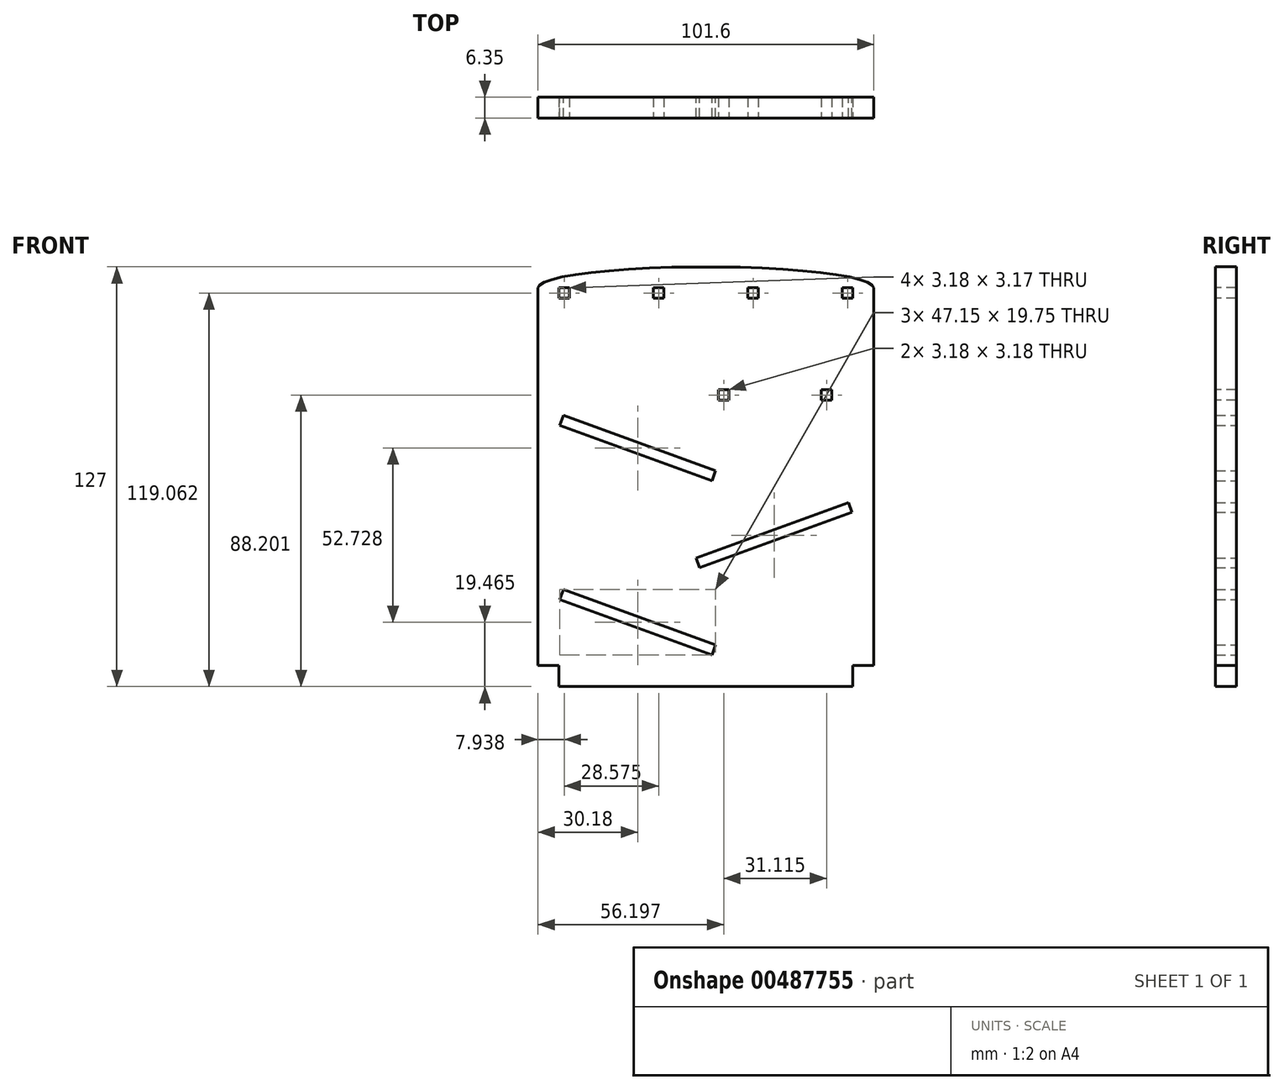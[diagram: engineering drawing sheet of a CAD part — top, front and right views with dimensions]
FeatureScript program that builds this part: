
annotation { "Feature Type Name" : "Feature", "Feature Type Description" : "" }
export const myFeature = defineFeature(function(context is Context, id is Id, definition is map)
    precondition{}
    {
        {
            var Q0;
            Q0=qCreatedBy(makeId("Front.planeOp"),FACE);
            var sketch = newSketch(context, id + "F0", { "sketchPlane" : qUnion([Q0])});
            skLineSegment(sketch, "E0.bottom", {"start": v(-50.8, 63.5) * mm, "end": v(50.8, 63.5) * mm});
            skLineSegment(sketch, "E0.top", {"start": v(-50.8, -63.5) * mm, "end": v(50.8, -63.5) * mm});
            skLineSegment(sketch, "E0.left", {"start": v(-50.8, 63.5) * mm, "end": v(-50.8, -63.5) * mm});
            skLineSegment(sketch, "E0.right", {"start": v(50.8, 63.5) * mm, "end": v(50.8, -63.5) * mm});
            skPoint(sketch, "E0.middle", {"position": v(0, 0) * mm});
            skSolve(sketch);
        }
        {
            var Q0;
            Q0 = qSketchRegion(id + "F0", true);
            extrude(context, id + "F1", {"entities" : qUnion([Q0]), "depth" : 6.35 * mm});
        }
        {
            var Q0;
            Q0=makeQuery(id+"F1.opExtrude","CAP_FACE",FACE,{"disambiguationData":[OSD([sQuery(id+"F0.wireOp",EDGE,"E0.bottom"),sQuery(id+"F0.wireOp",EDGE,"E0.top"),sQuery(id+"F0.wireOp",EDGE,"E0.left"),sQuery(id+"F0.wireOp",EDGE,"E0.right")])],"isStart":false});
            var sketch = newSketch(context, id + "F2", { "sketchPlane" : qUnion([Q0])});
            skLineSegment(sketch, "E1.bottom", {"start": v(-50.8, 63.5) * mm, "end": v(50.8, 63.5) * mm});
            skLineSegment(sketch, "E1.top", {"start": v(-50.8, 57.15) * mm, "end": v(50.8, 57.15) * mm});
            skLineSegment(sketch, "E1.left", {"start": v(-50.8, 63.5) * mm, "end": v(-50.8, 57.15) * mm});
            skLineSegment(sketch, "E1.right", {"start": v(50.8, 63.5) * mm, "end": v(50.8, 57.15) * mm});
            skLineSegment(sketch, "E2.bottom", {"start": v(-50.8, 57.15) * mm, "end": v(-44.45, 57.15) * mm});
            skLineSegment(sketch, "E2.top", {"start": v(-50.8, 50.8) * mm, "end": v(-44.45, 50.8) * mm});
            skLineSegment(sketch, "E2.left", {"start": v(-50.8, 57.15) * mm, "end": v(-50.8, 50.8) * mm});
            skLineSegment(sketch, "E2.right", {"start": v(-44.45, 57.15) * mm, "end": v(-44.45, 50.8) * mm});
            skLineSegment(sketch, "E3.bottom", {"start": v(-50.8, -63.5) * mm, "end": v(-44.45, -63.5) * mm});
            skLineSegment(sketch, "E3.top", {"start": v(-50.8, -57.15) * mm, "end": v(-44.45, -57.15) * mm});
            skLineSegment(sketch, "E3.left", {"start": v(-50.8, -63.5) * mm, "end": v(-50.8, -57.15) * mm});
            skLineSegment(sketch, "E3.right", {"start": v(-44.45, -63.5) * mm, "end": v(-44.45, -57.15) * mm});
            skLineSegment(sketch, "E4.bottom", {"start": v(50.8, -63.5) * mm, "end": v(44.45, -63.5) * mm});
            skLineSegment(sketch, "E4.top", {"start": v(50.8, -57.15) * mm, "end": v(44.45, -57.15) * mm});
            skLineSegment(sketch, "E4.left", {"start": v(50.8, -63.5) * mm, "end": v(50.8, -57.15) * mm});
            skLineSegment(sketch, "E4.right", {"start": v(44.45, -63.5) * mm, "end": v(44.45, -57.15) * mm});
            skLineSegment(sketch, "E5.bottom", {"start": v(50.8, 57.15) * mm, "end": v(44.45, 57.15) * mm});
            skLineSegment(sketch, "E5.top", {"start": v(50.8, 50.8) * mm, "end": v(44.45, 50.8) * mm});
            skLineSegment(sketch, "E5.left", {"start": v(50.8, 57.15) * mm, "end": v(50.8, 50.8) * mm});
            skLineSegment(sketch, "E5.right", {"start": v(44.45, 57.15) * mm, "end": v(44.45, 50.8) * mm});
            skSolve(sketch);
        }
        {
            var Q0;
            Q0=makeQuery(id+"F2.imprint","IMPRINT",FACE,{"disambiguationData":[TD([[makeQuery(id+"F2.imprint","IMPRINT",EDGE,{"derivedFrom":sQuery(id+"F2.wireOp",EDGE,"E2.bottom")}),-1.0]])]});
            var Q1;
            Q1=makeQuery(id+"F2.imprint","IMPRINT",FACE,{"disambiguationData":[TD([[makeQuery(id+"F2.imprint","IMPRINT",EDGE,{"derivedFrom":sQuery(id+"F2.wireOp",EDGE,"E5.bottom")}),1.0]])]});
            var Q2;
            Q2=makeQuery(id+"F2.imprint","IMPRINT",FACE,{"disambiguationData":[TD([[makeQuery(id+"F2.imprint","IMPRINT",EDGE,{"derivedFrom":sQuery(id+"F2.wireOp",EDGE,"E4.bottom")}),1.0]])]});
            var Q3;
            Q3=makeQuery(id+"F2.imprint","IMPRINT",FACE,{"disambiguationData":[TD([[makeQuery(id+"F2.imprint","IMPRINT",EDGE,{"derivedFrom":sQuery(id+"F2.wireOp",EDGE,"E3.bottom")}),1.0]])]});
            extrude(context, id + "F3", {"entities" : qUnion([Q0, Q1, Q2, Q3]), "operationType" : NewBodyOperationType.REMOVE, "endBound" : BoundingType.THROUGH_ALL, "oppositeDirection" : true, "depth" : 6.35 * mm});
        }
        {
            var Q0;
            Q0=makeQuery(id+"F1.opExtrude","CAP_FACE",FACE,{"disambiguationData":[OSD([sQuery(id+"F0.wireOp",EDGE,"E0.bottom"),sQuery(id+"F0.wireOp",EDGE,"E0.top"),sQuery(id+"F0.wireOp",EDGE,"E0.left"),sQuery(id+"F0.wireOp",EDGE,"E0.right")])],"isStart":false});
            var sketch = newSketch(context, id + "F4", { "sketchPlane" : qUnion([Q0])});
            skLineSegment(sketch, "E6.bottom", {"start": v(-44.45, 57.15) * mm, "end": v(44.45, 57.15) * mm});
            skLineSegment(sketch, "E6.top", {"start": v(-44.45, 50.8) * mm, "end": v(44.45, 50.8) * mm});
            skLineSegment(sketch, "E6.left", {"start": v(-44.45, 57.15) * mm, "end": v(-44.45, 50.8) * mm});
            skLineSegment(sketch, "E6.right", {"start": v(44.45, 57.15) * mm, "end": v(44.45, 50.8) * mm});
            skEllipse(sketch, "E7", {"center": v(0, 57.15) * mm, "majorRadius": 50.8 * mm, "minorRadius": 6.35 * mm, "majorAxis": v(-1, 0)});
            skSolve(sketch);
        }
        {
            var Q0;
            {var subQ1=sQuery(id+"F0.wireOp",EDGE,"E0.bottom");var subQ2=sQuery(id+"F0.wireOp",EDGE,"E0.left");var subQ4=makeQuery(id+"F3.boolean.opBoolean","SPLIT",EDGE,{"disambiguationData":[TD([makeQuery(id+"F1.opExtrude","SWEPT_FACE",FACE,{"disambiguationData":[OSD([subQ1])]})])],"derivedFrom":makeQuery(id+"F1.opExtrude","CAP_EDGE",EDGE,{"disambiguationData":[OSD([subQ2])],"isStart":false})});Q0=makeQuery(id+"F4.imprint","IMPRINT",FACE,{"disambiguationData":[TD([[makeQuery(id+"F4.imprint","IMPRINT",EDGE,{"derivedFrom":subQ4}),1.0]])]});}
            var Q1;
            {var subQ1=sQuery(id+"F0.wireOp",EDGE,"E0.bottom");var subQ2=sQuery(id+"F0.wireOp",EDGE,"E0.right");var subQ4=makeQuery(id+"F3.boolean.opBoolean","SPLIT",EDGE,{"disambiguationData":[TD([makeQuery(id+"F1.opExtrude","SWEPT_FACE",FACE,{"disambiguationData":[OSD([subQ1])]})])],"derivedFrom":makeQuery(id+"F1.opExtrude","CAP_EDGE",EDGE,{"disambiguationData":[OSD([subQ2])],"isStart":false})});Q1=makeQuery(id+"F4.imprint","IMPRINT",FACE,{"disambiguationData":[TD([[makeQuery(id+"F4.imprint","IMPRINT",EDGE,{"derivedFrom":subQ4}),-1.0]])]});}
            extrude(context, id + "F5", {"entities" : qUnion([Q0, Q1]), "operationType" : NewBodyOperationType.REMOVE, "endBound" : BoundingType.THROUGH_ALL, "oppositeDirection" : true, "depth" : 25.4 * mm});
        }
        {
            var Q0;
            Q0=makeQuery(id+"F1.opExtrude","CAP_FACE",FACE,{"disambiguationData":[OSD([sQuery(id+"F0.wireOp",EDGE,"E0.bottom"),sQuery(id+"F0.wireOp",EDGE,"E0.top"),sQuery(id+"F0.wireOp",EDGE,"E0.left"),sQuery(id+"F0.wireOp",EDGE,"E0.right")])],"isStart":false});
            var sketch = newSketch(context, id + "F6", { "sketchPlane" : qUnion([Q0])});
            skPoint(sketch, "E8.oppositeSnap0", {"position": v(-44.45, 53.98) * mm});
            skLineSegment(sketch, "E8.bottom", {"start": v(-44.45, 57.15) * mm, "end": v(-41.28, 57.15) * mm});
            skLineSegment(sketch, "E8.top", {"start": v(-44.45, 53.98) * mm, "end": v(-41.28, 53.98) * mm});
            skLineSegment(sketch, "E8.left", {"start": v(-44.45, 57.15) * mm, "end": v(-44.45, 53.98) * mm});
            skLineSegment(sketch, "E8.right", {"start": v(-41.28, 57.15) * mm, "end": v(-41.28, 53.98) * mm});
            skLineSegment(sketch, "E9.bottom", {"start": v(-15.87, 57.15) * mm, "end": v(-12.7, 57.15) * mm});
            skLineSegment(sketch, "E9.top", {"start": v(-15.87, 53.98) * mm, "end": v(-12.7, 53.98) * mm});
            skLineSegment(sketch, "E9.left", {"start": v(-15.87, 57.15) * mm, "end": v(-15.87, 53.98) * mm});
            skLineSegment(sketch, "E9.right", {"start": v(-12.7, 57.15) * mm, "end": v(-12.7, 53.98) * mm});
            skLineSegment(sketch, "E10.bottom", {"start": v(12.7, 57.15) * mm, "end": v(15.88, 57.15) * mm});
            skLineSegment(sketch, "E10.top", {"start": v(12.7, 53.98) * mm, "end": v(15.88, 53.98) * mm});
            skLineSegment(sketch, "E10.left", {"start": v(12.7, 57.15) * mm, "end": v(12.7, 53.98) * mm});
            skLineSegment(sketch, "E10.right", {"start": v(15.88, 57.15) * mm, "end": v(15.88, 53.98) * mm});
            skLineSegment(sketch, "E11.bottom", {"start": v(41.28, 57.15) * mm, "end": v(44.45, 57.15) * mm});
            skLineSegment(sketch, "E11.top", {"start": v(41.28, 53.98) * mm, "end": v(44.45, 53.98) * mm});
            skLineSegment(sketch, "E11.left", {"start": v(41.28, 57.15) * mm, "end": v(41.28, 53.98) * mm});
            skLineSegment(sketch, "E11.right", {"start": v(44.45, 57.15) * mm, "end": v(44.45, 53.98) * mm});
            skLineSegment(sketch, "E12", {"start": v(6.99, 26.29) * mm, "end": v(34.93, 26.29) * mm});
            skLineSegment(sketch, "E13.bottom", {"start": v(34.93, 26.29) * mm, "end": v(38.1, 26.29) * mm});
            skLineSegment(sketch, "E13.top", {"start": v(34.93, 23.11) * mm, "end": v(38.1, 23.11) * mm});
            skLineSegment(sketch, "E13.left", {"start": v(34.93, 26.29) * mm, "end": v(34.93, 23.11) * mm});
            skLineSegment(sketch, "E13.right", {"start": v(38.1, 26.29) * mm, "end": v(38.1, 23.11) * mm});
            skLineSegment(sketch, "E14.bottom", {"start": v(6.99, 26.29) * mm, "end": v(3.8, 26.29) * mm});
            skLineSegment(sketch, "E14.top", {"start": v(6.99, 23.11) * mm, "end": v(3.81, 23.11) * mm});
            skLineSegment(sketch, "E14.left", {"start": v(6.99, 26.29) * mm, "end": v(6.99, 23.11) * mm});
            skLineSegment(sketch, "E14.right", {"start": v(3.8, 26.29) * mm, "end": v(3.81, 23.11) * mm});
            skSolve(sketch);
        }
        {
            var Q0;
            Q0=makeQuery(id+"F6.imprint","IMPRINT",FACE,{"disambiguationData":[TD([[makeQuery(id+"F6.imprint","IMPRINT",EDGE,{"derivedFrom":sQuery(id+"F6.wireOp",EDGE,"E8.bottom")}),-1.0]])]});
            var Q1;
            Q1=makeQuery(id+"F6.imprint","IMPRINT",FACE,{"disambiguationData":[TD([[makeQuery(id+"F6.imprint","IMPRINT",EDGE,{"derivedFrom":sQuery(id+"F6.wireOp",EDGE,"E9.bottom")}),-1.0]])]});
            var Q2;
            Q2=makeQuery(id+"F6.imprint","IMPRINT",FACE,{"disambiguationData":[TD([[makeQuery(id+"F6.imprint","IMPRINT",EDGE,{"derivedFrom":sQuery(id+"F6.wireOp",EDGE,"E10.bottom")}),-1.0]])]});
            var Q3;
            Q3=makeQuery(id+"F6.imprint","IMPRINT",FACE,{"disambiguationData":[TD([[makeQuery(id+"F6.imprint","IMPRINT",EDGE,{"derivedFrom":sQuery(id+"F6.wireOp",EDGE,"E11.bottom")}),-1.0]])]});
            var Q4;
            Q4=makeQuery(id+"F6.imprint","IMPRINT",FACE,{"disambiguationData":[TD([[makeQuery(id+"F6.imprint","IMPRINT",EDGE,{"derivedFrom":sQuery(id+"F6.wireOp",EDGE,"E13.bottom")}),-1.0]])]});
            var Q5;
            Q5=makeQuery(id+"F6.imprint","IMPRINT",FACE,{"disambiguationData":[TD([[makeQuery(id+"F6.imprint","IMPRINT",EDGE,{"derivedFrom":sQuery(id+"F6.wireOp",EDGE,"E14.bottom")}),1.0]])]});
            extrude(context, id + "F7", {"entities" : qUnion([Q0, Q1, Q2, Q3, Q4, Q5]), "operationType" : NewBodyOperationType.REMOVE, "endBound" : BoundingType.THROUGH_ALL, "oppositeDirection" : true, "depth" : 25.4 * mm});
        }
        {
            var Q0;
            Q0=qCreatedBy(makeId("Front.planeOp"),FACE);
            var sketch = newSketch(context, id + "F8", { "sketchPlane" : qUnion([Q0])});
            skLineSegment(sketch, "E15", {"start": v(-43.11, 18.57) * mm, "end": v(2.96, 1.8) * mm});
            skLineSegment(sketch, "E16", {"start": v(2.96, 1.8) * mm, "end": v(1.87, -1.18) * mm});
            skLineSegment(sketch, "E17", {"start": v(1.87, -1.18) * mm, "end": v(-44.2, 15.58) * mm});
            skLineSegment(sketch, "E18", {"start": v(-44.2, 15.58) * mm, "end": v(-43.11, 18.57) * mm});
            skSolve(sketch);
        }
        {
            var Q0;
            Q0 = qSketchRegion(id + "F8", true);
            extrude(context, id + "F9", {"entities" : qUnion([Q0]), "operationType" : NewBodyOperationType.REMOVE, "depth" : 34.8 * mm});
        }
        {
            var Q0;
            Q0=qCreatedBy(makeId("Front.planeOp"),FACE);
            var sketch = newSketch(context, id + "F10", { "sketchPlane" : qUnion([Q0])});
            skLineSegment(sketch, "E19", {"start": v(-2.96, -24.56) * mm, "end": v(43.11, -7.8) * mm});
            skLineSegment(sketch, "E20", {"start": v(43.11, -7.8) * mm, "end": v(44.2, -10.78) * mm});
            skLineSegment(sketch, "E21", {"start": v(44.2, -10.78) * mm, "end": v(-1.87, -27.55) * mm});
            skLineSegment(sketch, "E22", {"start": v(-1.87, -27.55) * mm, "end": v(-2.96, -24.56) * mm});
            skSolve(sketch);
        }
        {
            var Q0;
            Q0 = qSketchRegion(id + "F10", true);
            extrude(context, id + "F11", {"entities" : qUnion([Q0]), "operationType" : NewBodyOperationType.REMOVE, "depth" : 25.4 * mm});
        }
        {
            var Q0;
            Q0=qCreatedBy(makeId("Front.planeOp"),FACE);
            var sketch = newSketch(context, id + "F12", { "sketchPlane" : qUnion([Q0])});
            skLineSegment(sketch, "E23", {"start": v(-43.11, -34.16) * mm, "end": v(2.96, -50.93) * mm});
            skLineSegment(sketch, "E24", {"start": v(-43.11, -34.16) * mm, "end": v(-44.2, -37.14) * mm});
            skLineSegment(sketch, "E25", {"start": v(-44.2, -37.14) * mm, "end": v(1.87, -53.91) * mm});
            skLineSegment(sketch, "E26", {"start": v(1.87, -53.91) * mm, "end": v(2.96, -50.93) * mm});
            skSolve(sketch);
        }
        {
            var Q0;
            Q0 = qSketchRegion(id + "F12", true);
            extrude(context, id + "F13", {"entities" : qUnion([Q0]), "operationType" : NewBodyOperationType.REMOVE, "depth" : 25.4 * mm});
        }
    });
